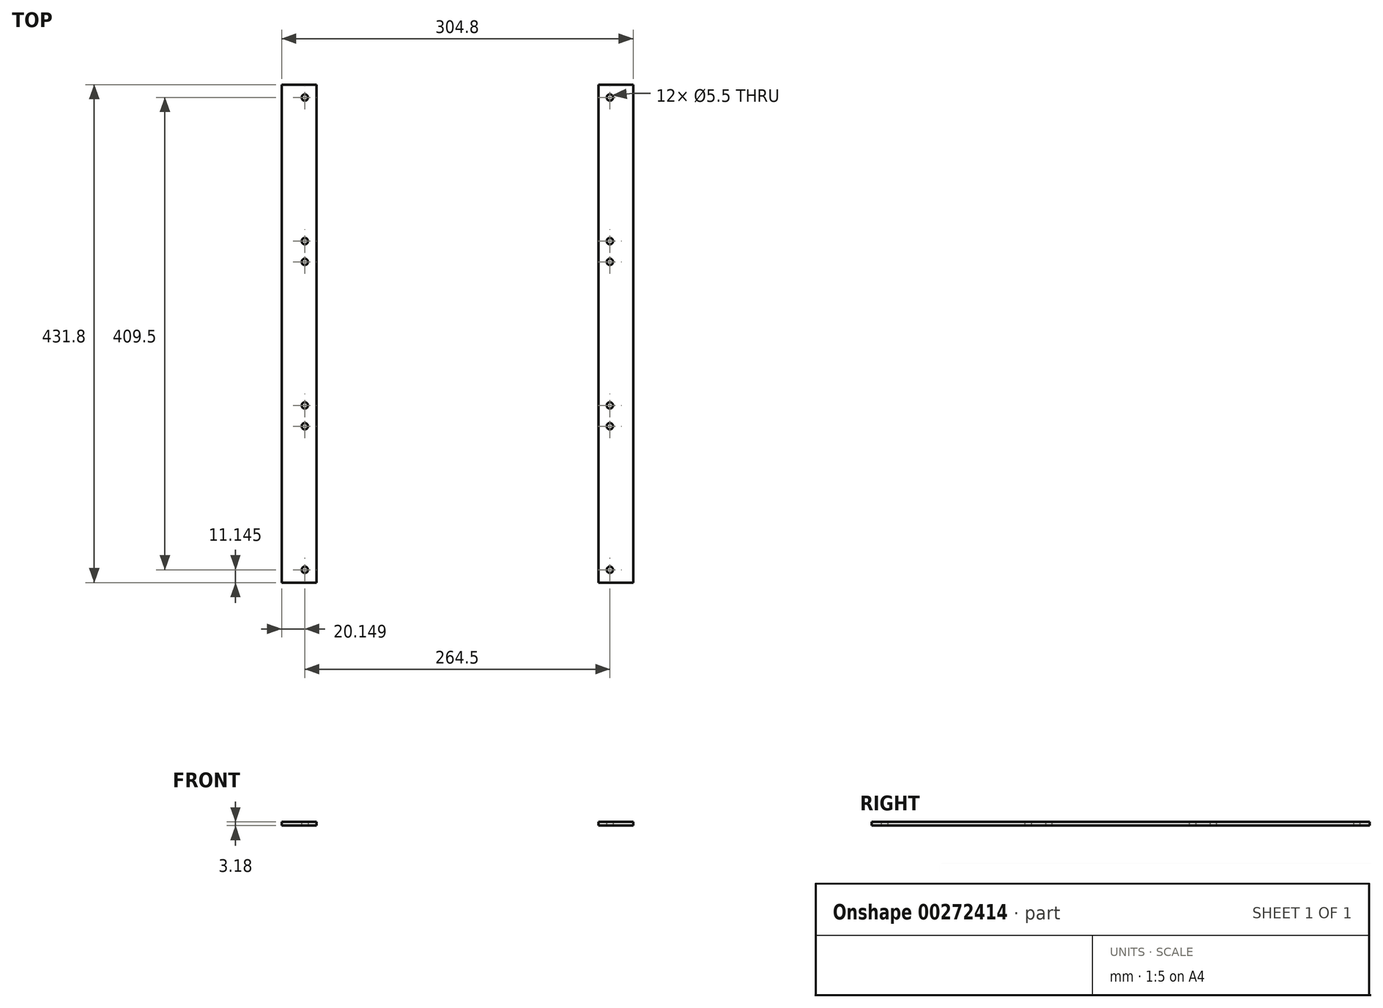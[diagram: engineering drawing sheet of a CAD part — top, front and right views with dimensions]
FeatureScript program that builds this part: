
annotation { "Feature Type Name" : "Feature", "Feature Type Description" : "" }
export const myFeature = defineFeature(function(context is Context, id is Id, definition is map)
    precondition{}
    {
        {
            var Q0;
            Q0=qCreatedBy(makeId("Top.planeOp"),FACE);
            var sketch = newSketch(context, id + "F0", { "sketchPlane" : qUnion([Q0])});
            skLineSegment(sketch, "E0.bottom", {"start": v(-344.24, 247.34) * mm, "end": v(-314.1, 247.34) * mm});
            skLineSegment(sketch, "E0.top", {"start": v(-344.24, -184.46) * mm, "end": v(-314.1, -184.46) * mm});
            skLineSegment(sketch, "E0.left", {"start": v(-344.24, 247.34) * mm, "end": v(-344.24, -184.46) * mm});
            skLineSegment(sketch, "E0.right", {"start": v(-314.1, 247.34) * mm, "end": v(-314.1, -184.46) * mm});
            skLineSegment(sketch, "E1.bottom", {"start": v(-39.44, 247.34) * mm, "end": v(-69.6, 247.34) * mm});
            skLineSegment(sketch, "E1.top", {"start": v(-39.44, -184.46) * mm, "end": v(-69.6, -184.46) * mm});
            skLineSegment(sketch, "E1.left", {"start": v(-39.44, 247.34) * mm, "end": v(-39.44, -184.46) * mm});
            skLineSegment(sketch, "E1.right", {"start": v(-69.6, 247.34) * mm, "end": v(-69.6, -184.46) * mm});
            skPoint(sketch, "E2", {"position": v(-324.1, -173.31) * mm});
            skPoint(sketch, "E3", {"position": v(-324.1, -48.81) * mm});
            skPoint(sketch, "E4", {"position": v(-324.1, -30.81) * mm});
            skPoint(sketch, "E5", {"position": v(-324.1, 93.69) * mm});
            skPoint(sketch, "E6", {"position": v(-324.1, 111.69) * mm});
            skPoint(sketch, "E7", {"position": v(-324.1, 236.19) * mm});
            skPoint(sketch, "E8", {"position": v(-317.63, 250.19) * mm});
            skLineSegment(sketch, "E9", {"start": v(-324.1, 236.19) * mm, "end": v(-324.1, 247.34) * mm, "construction": true});
            skLineSegment(sketch, "E10", {"start": v(-324.1, -173.31) * mm, "end": v(-324.1, -184.46) * mm, "construction": true});
            skPoint(sketch, "E11", {"position": v(-191.84, -184.46) * mm});
            skLineSegment(sketch, "E12", {"start": v(-191.84, -184.46) * mm, "end": v(-191.84, 139.98) * mm, "construction": true});
            skPoint(sketch, "E13.MirrorP", {"position": v(-59.6, -173.31) * mm});
            skPoint(sketch, "E14.MirrorP", {"position": v(-59.6, -48.81) * mm});
            skPoint(sketch, "E15.MirrorP", {"position": v(-59.6, -30.81) * mm});
            skPoint(sketch, "E16.MirrorP", {"position": v(-59.6, 93.69) * mm});
            skPoint(sketch, "E17.MirrorP", {"position": v(-59.6, 111.69) * mm});
            skPoint(sketch, "E18.MirrorP", {"position": v(-59.6, 236.19) * mm});
            skCircle(sketch, "E19", {"center": v(-59.6, -173.31) * mm, "radius": 2.75 * mm});
            skCircle(sketch, "E20", {"center": v(-59.6, -48.81) * mm, "radius": 2.75 * mm});
            skCircle(sketch, "E21", {"center": v(-59.6, -30.81) * mm, "radius": 2.75 * mm});
            skCircle(sketch, "E22", {"center": v(-59.6, 93.69) * mm, "radius": 2.75 * mm});
            skCircle(sketch, "E23", {"center": v(-59.6, 111.69) * mm, "radius": 2.75 * mm});
            skCircle(sketch, "E24", {"center": v(-59.6, 236.19) * mm, "radius": 2.75 * mm});
            skCircle(sketch, "E25", {"center": v(-324.1, 236.19) * mm, "radius": 2.75 * mm});
            skCircle(sketch, "E26", {"center": v(-324.1, 111.69) * mm, "radius": 2.75 * mm});
            skCircle(sketch, "E27", {"center": v(-324.1, 93.69) * mm, "radius": 2.75 * mm});
            skCircle(sketch, "E28", {"center": v(-324.1, -30.81) * mm, "radius": 2.75 * mm});
            skCircle(sketch, "E29", {"center": v(-324.1, -48.81) * mm, "radius": 2.75 * mm});
            skCircle(sketch, "E30", {"center": v(-324.1, -173.31) * mm, "radius": 2.75 * mm});
            skLineSegment(sketch, "E31", {"start": v(-324.1, -173.31) * mm, "end": v(-59.6, -173.31) * mm, "construction": true});
            skLineSegment(sketch, "E32", {"start": v(-59.6, -173.31) * mm, "end": v(-59.6, -184.46) * mm, "construction": true});
            skLineSegment(sketch, "E33", {"start": v(-59.6, -173.31) * mm, "end": v(-69.6, -173.31) * mm, "construction": true});
            skSolve(sketch);
        }
        {
            var Q0;
            Q0 = qSketchRegion(id + "F0", true);
            extrude(context, id + "F1", {"entities" : qUnion([Q0]), "depth" : 3.17 * mm});
        }
    });
